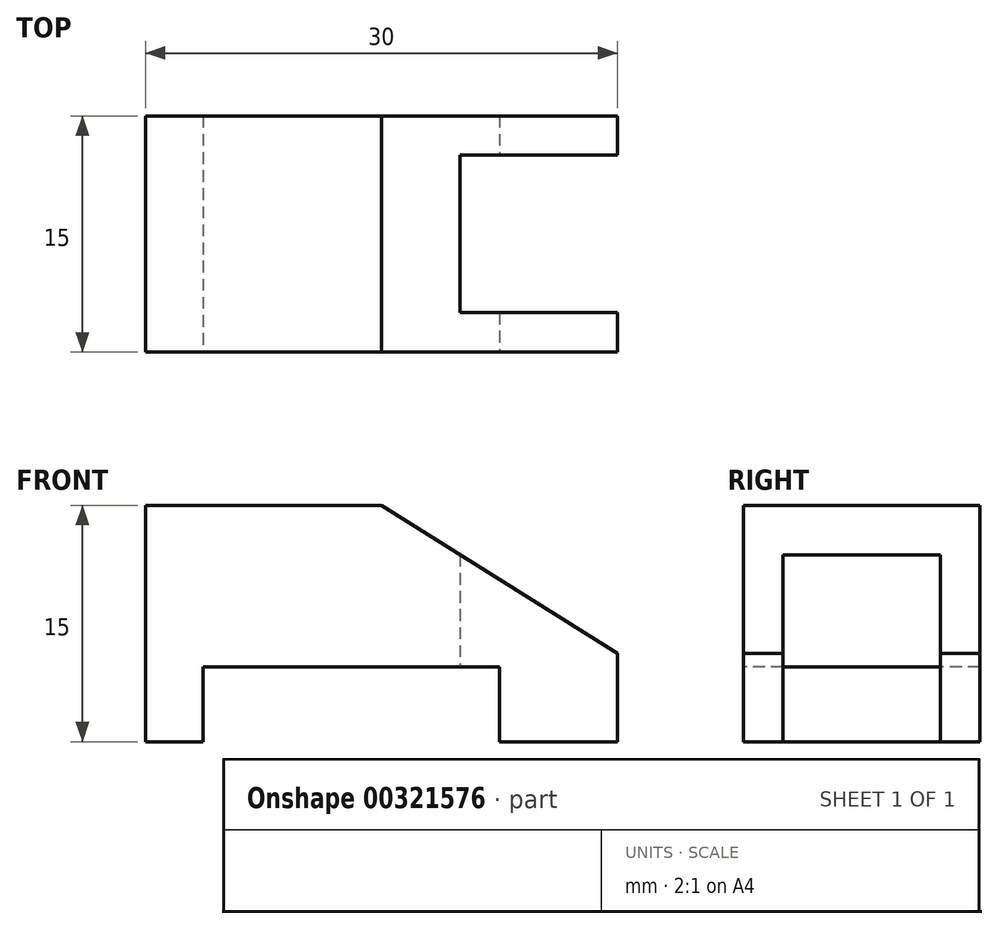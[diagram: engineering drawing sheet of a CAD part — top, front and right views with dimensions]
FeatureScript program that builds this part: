
annotation { "Feature Type Name" : "Feature", "Feature Type Description" : "" }
export const myFeature = defineFeature(function(context is Context, id is Id, definition is map)
    precondition{}
    {
        {
            var Q0;
            Q0=qCreatedBy(makeId("Top.planeOp"),FACE);
            var sketch = newSketch(context, id + "F0", { "sketchPlane" : qUnion([Q0])});
            skLineSegment(sketch, "E0", {"start": v(0, 0) * mm, "end": v(0, 15) * mm});
            skLineSegment(sketch, "E1", {"start": v(0, 15) * mm, "end": v(30, 15) * mm});
            skLineSegment(sketch, "E2", {"start": v(30, 15) * mm, "end": v(30, 12.5) * mm});
            skLineSegment(sketch, "E3", {"start": v(30, 12.5) * mm, "end": v(20, 12.5) * mm});
            skLineSegment(sketch, "E4", {"start": v(20, 12.5) * mm, "end": v(20, 2.5) * mm});
            skLineSegment(sketch, "E5", {"start": v(20, 2.5) * mm, "end": v(30, 2.5) * mm});
            skLineSegment(sketch, "E6", {"start": v(30, 2.5) * mm, "end": v(30, 0) * mm});
            skLineSegment(sketch, "E7", {"start": v(30, 0) * mm, "end": v(0, 0) * mm});
            skSolve(sketch);
        }
        {
            var Q0;
            Q0 = qSketchRegion(id + "F0", true);
            extrude(context, id + "F1", {"entities" : qUnion([Q0]), "depth" : 15 * mm});
        }
        {
            var Q0;
            Q0=makeQuery(id+"F1.opExtrude","SWEPT_FACE",FACE,{"disambiguationData":[OSD([sQuery(id+"F0.wireOp",EDGE,"E7")])]});
            var sketch = newSketch(context, id + "F2", { "sketchPlane" : qUnion([Q0])});
            skLineSegment(sketch, "E8", {"start": v(15, 15) * mm, "end": v(30, 5.6) * mm});
            skLineSegment(sketch, "E9", {"start": v(30, 5.6) * mm, "end": v(30, 15) * mm});
            skLineSegment(sketch, "E10", {"start": v(30, 15) * mm, "end": v(15, 15) * mm});
            skLineSegment(sketch, "E11", {"start": v(3.67, 0) * mm, "end": v(3.67, 4.75) * mm});
            skLineSegment(sketch, "E12", {"start": v(3.67, 4.75) * mm, "end": v(22.5, 4.75) * mm});
            skPoint(sketch, "E12.endSnap0", {"position": v(22.5, 10.3) * mm});
            skLineSegment(sketch, "E13", {"start": v(22.5, 4.75) * mm, "end": v(22.5, 0) * mm});
            skLineSegment(sketch, "E14", {"start": v(22.5, 0) * mm, "end": v(3.67, 0) * mm});
            skSolve(sketch);
        }
        {
            var Q0;
            Q0=makeQuery(id+"F2.imprint","IMPRINT",FACE,{"disambiguationData":[TD([[makeQuery(id+"F2.imprint","IMPRINT",EDGE,{"derivedFrom":sQuery(id+"F2.wireOp",EDGE,"E8")}),1.0]])]});
            extrude(context, id + "F3", {"entities" : qUnion([Q0]), "operationType" : NewBodyOperationType.REMOVE, "endBound" : BoundingType.THROUGH_ALL, "oppositeDirection" : true, "depth" : 25 * mm});
        }
        {
            var Q0;
            Q0=makeQuery(id+"F2.imprint","IMPRINT",FACE,{"disambiguationData":[TD([[makeQuery(id+"F2.imprint","IMPRINT",EDGE,{"derivedFrom":sQuery(id+"F2.wireOp",EDGE,"E11")}),-1.0]])]});
            extrude(context, id + "F4", {"entities" : qUnion([Q0]), "operationType" : NewBodyOperationType.REMOVE, "endBound" : BoundingType.THROUGH_ALL, "oppositeDirection" : true, "depth" : 25 * mm});
        }
    });
